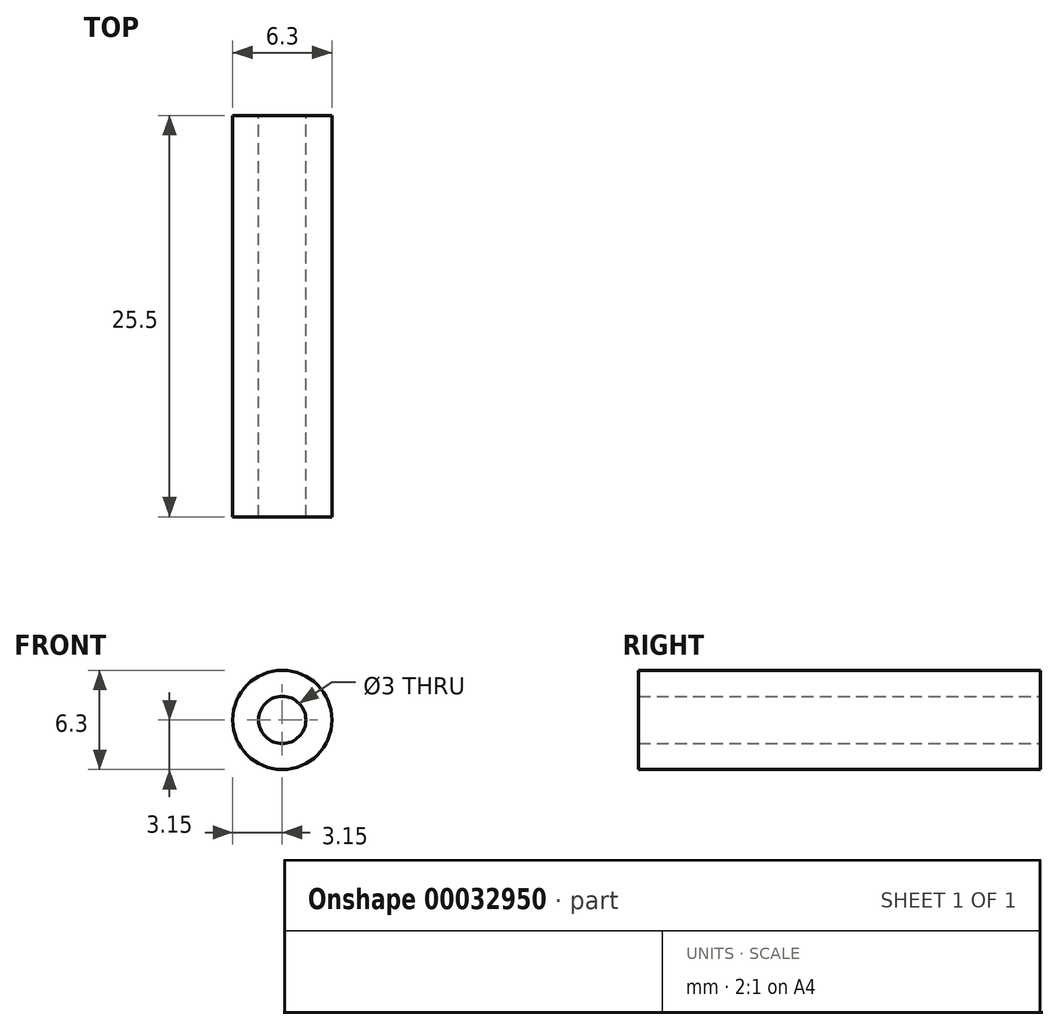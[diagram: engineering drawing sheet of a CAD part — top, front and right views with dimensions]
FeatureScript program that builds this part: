
annotation { "Feature Type Name" : "Feature", "Feature Type Description" : "" }
export const myFeature = defineFeature(function(context is Context, id is Id, definition is map)
    precondition{}
    {
        {
            var Q0;
            Q0=qCreatedBy(makeId("Front.planeOp"),FACE);
            var sketch = newSketch(context, id + "F0", { "sketchPlane" : qUnion([Q0])});
            skCircle(sketch, "E0", {"center": v(0, 0) * mm, "radius": 1.5 * mm});
            skCircle(sketch, "E1", {"center": v(0, 0) * mm, "radius": 3.15 * mm});
            skSolve(sketch);
        }
        {
            var Q0;
            Q0 = qSketchRegion(id + "F0", true);
            extrude(context, id + "F1", {"entities" : qUnion([Q0]), "depth" : 25.5 * mm});
        }
    });
